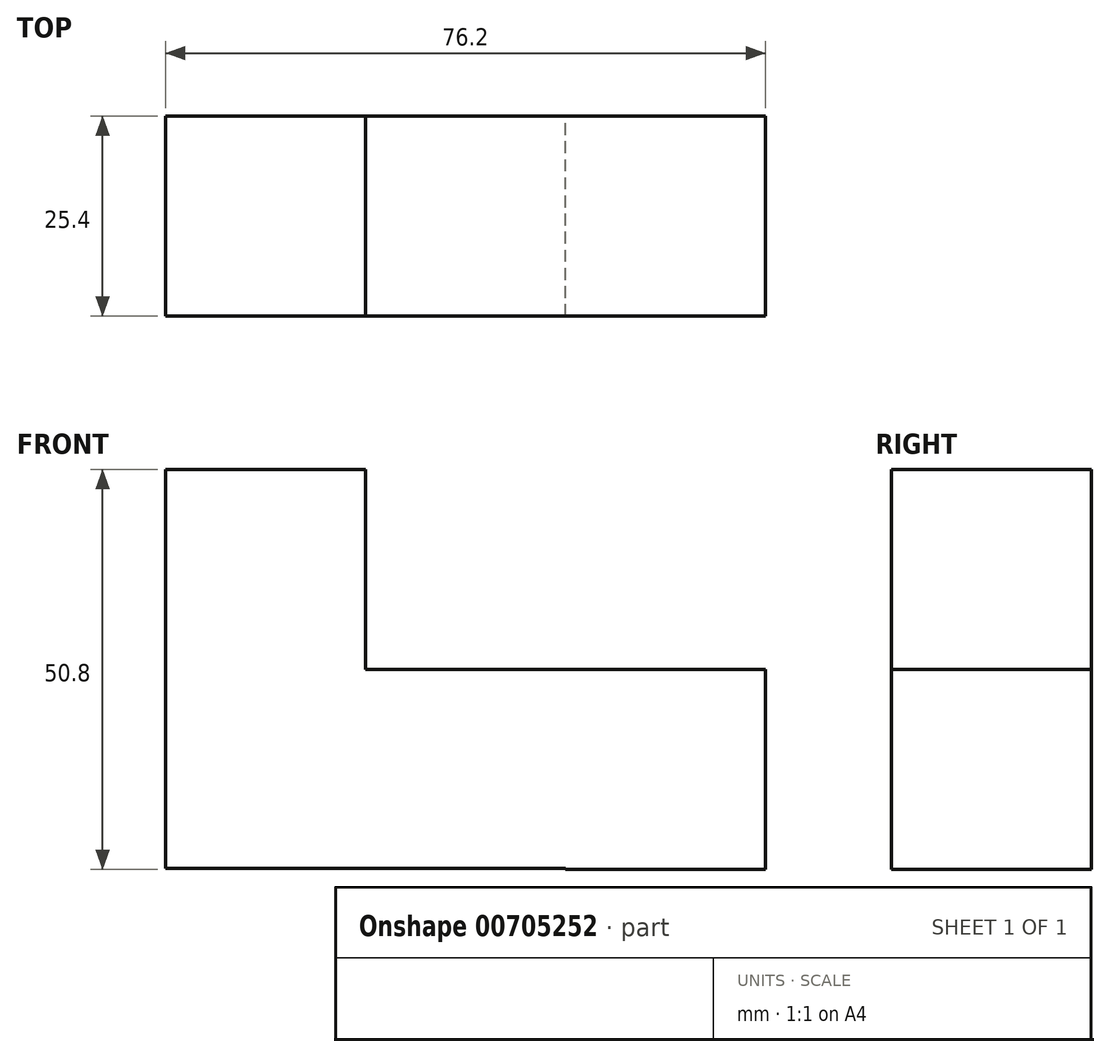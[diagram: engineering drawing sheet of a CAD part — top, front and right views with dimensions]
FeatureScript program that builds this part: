
annotation { "Feature Type Name" : "Feature", "Feature Type Description" : "" }
export const myFeature = defineFeature(function(context is Context, id is Id, definition is map)
    precondition{}
    {
        {
            var Q0;
            Q0=qCreatedBy(makeId("Front.planeOp"),FACE);
            var sketch = newSketch(context, id + "F0", { "sketchPlane" : qUnion([Q0])});
            skLineSegment(sketch, "E0.bottom", {"start": v(0, 0) * mm, "end": v(25.4, 0) * mm});
            skLineSegment(sketch, "E0.top", {"start": v(0, -25.4) * mm, "end": v(25.4, -25.4) * mm});
            skLineSegment(sketch, "E0.left", {"start": v(0, 0) * mm, "end": v(0, -25.4) * mm});
            skLineSegment(sketch, "E0.right", {"start": v(25.4, 0) * mm, "end": v(25.4, -25.4) * mm});
            skLineSegment(sketch, "E1.bottom", {"start": v(0, 0) * mm, "end": v(-25.4, 0) * mm});
            skLineSegment(sketch, "E1.top", {"start": v(0, -25.28) * mm, "end": v(-25.4, -25.28) * mm});
            skLineSegment(sketch, "E1.left", {"start": v(0, 0) * mm, "end": v(0, -25.28) * mm});
            skLineSegment(sketch, "E1.right", {"start": v(-25.4, 0) * mm, "end": v(-25.4, -25.28) * mm});
            skLineSegment(sketch, "E2.bottom", {"start": v(-25.4, 0) * mm, "end": v(-50.8, 0) * mm});
            skLineSegment(sketch, "E2.top", {"start": v(-25.4, -25.28) * mm, "end": v(-50.8, -25.28) * mm});
            skLineSegment(sketch, "E2.right", {"start": v(-50.8, 0) * mm, "end": v(-50.8, -25.28) * mm});
            skLineSegment(sketch, "E3.top", {"start": v(-25.4, 25.4) * mm, "end": v(-50.8, 25.4) * mm});
            skLineSegment(sketch, "E3.left", {"start": v(-25.4, 0) * mm, "end": v(-25.4, 25.4) * mm});
            skLineSegment(sketch, "E3.right", {"start": v(-50.8, 0) * mm, "end": v(-50.8, 25.4) * mm});
            skLineSegment(sketch, "E4.bottom", {"start": v(-50.8, 25.4) * mm, "end": v(-25.4, 25.4) * mm});
            skLineSegment(sketch, "E4.top", {"start": v(-50.8, 50.8) * mm, "end": v(-25.4, 50.8) * mm});
            skLineSegment(sketch, "E4.left", {"start": v(-50.8, 25.4) * mm, "end": v(-50.8, 50.8) * mm});
            skLineSegment(sketch, "E4.right", {"start": v(-25.4, 25.4) * mm, "end": v(-25.4, 50.8) * mm});
            skLineSegment(sketch, "E5.bottom", {"start": v(25.4, 0) * mm, "end": v(0, 0) * mm});
            skLineSegment(sketch, "E5.top", {"start": v(25.4, 25.4) * mm, "end": v(0, 25.4) * mm});
            skLineSegment(sketch, "E5.left", {"start": v(25.4, 0) * mm, "end": v(25.4, 25.4) * mm});
            skLineSegment(sketch, "E5.right", {"start": v(0, 0) * mm, "end": v(0, 25.4) * mm});
            skSolve(sketch);
        }
        {
            var Q0;
            Q0=makeQuery(id+"F0.imprint","IMPRINT",FACE,{"disambiguationData":[TD([[makeQuery(id+"F0.imprint","IMPRINT",EDGE,{"derivedFrom":sQuery(id+"F0.wireOp",EDGE,"E4.bottom")}),1.0]])]});
            var Q1;
            Q1=makeQuery(id+"F0.imprint","IMPRINT",FACE,{"disambiguationData":[TD([[makeQuery(id+"F0.imprint","IMPRINT",EDGE,{"derivedFrom":sQuery(id+"F0.wireOp",EDGE,"E2.bottom")}),-1.0]])]});
            var Q2;
            Q2=makeQuery(id+"F0.imprint","IMPRINT",FACE,{"disambiguationData":[TD([[makeQuery(id+"F0.imprint","IMPRINT",EDGE,{"derivedFrom":sQuery(id+"F0.wireOp",EDGE,"E2.top")}),-1.0]])]});
            var Q3;
            Q3=makeQuery(id+"F0.imprint","IMPRINT",FACE,{"disambiguationData":[TD([[makeQuery(id+"F0.imprint","IMPRINT",EDGE,{"derivedFrom":sQuery(id+"F0.wireOp",EDGE,"E1.bottom")}),1.0]])]});
            var Q4;
            Q4=makeQuery(id+"F0.imprint","IMPRINT",FACE,{"disambiguationData":[TD([[makeQuery(id+"F0.imprint","IMPRINT",EDGE,{"derivedFrom":sQuery(id+"F0.wireOp",EDGE,"E0.top")}),1.0]])]});
            var Q5;
            Q5=makeQuery(id+"F0.imprint","IMPRINT",FACE,{"disambiguationData":[TD([[makeQuery(id+"F0.imprint","IMPRINT",EDGE,{"derivedFrom":sQuery(id+"F0.wireOp",EDGE,"E5.bottom")}),-1.0]])]});
            extrude(context, id + "F1", {"entities" : qUnion([Q0, Q1, Q2, Q3, Q4, Q5]), "depth" : 25.4 * mm, "offsetDistance" : 25.4 * mm});
        }
    });
